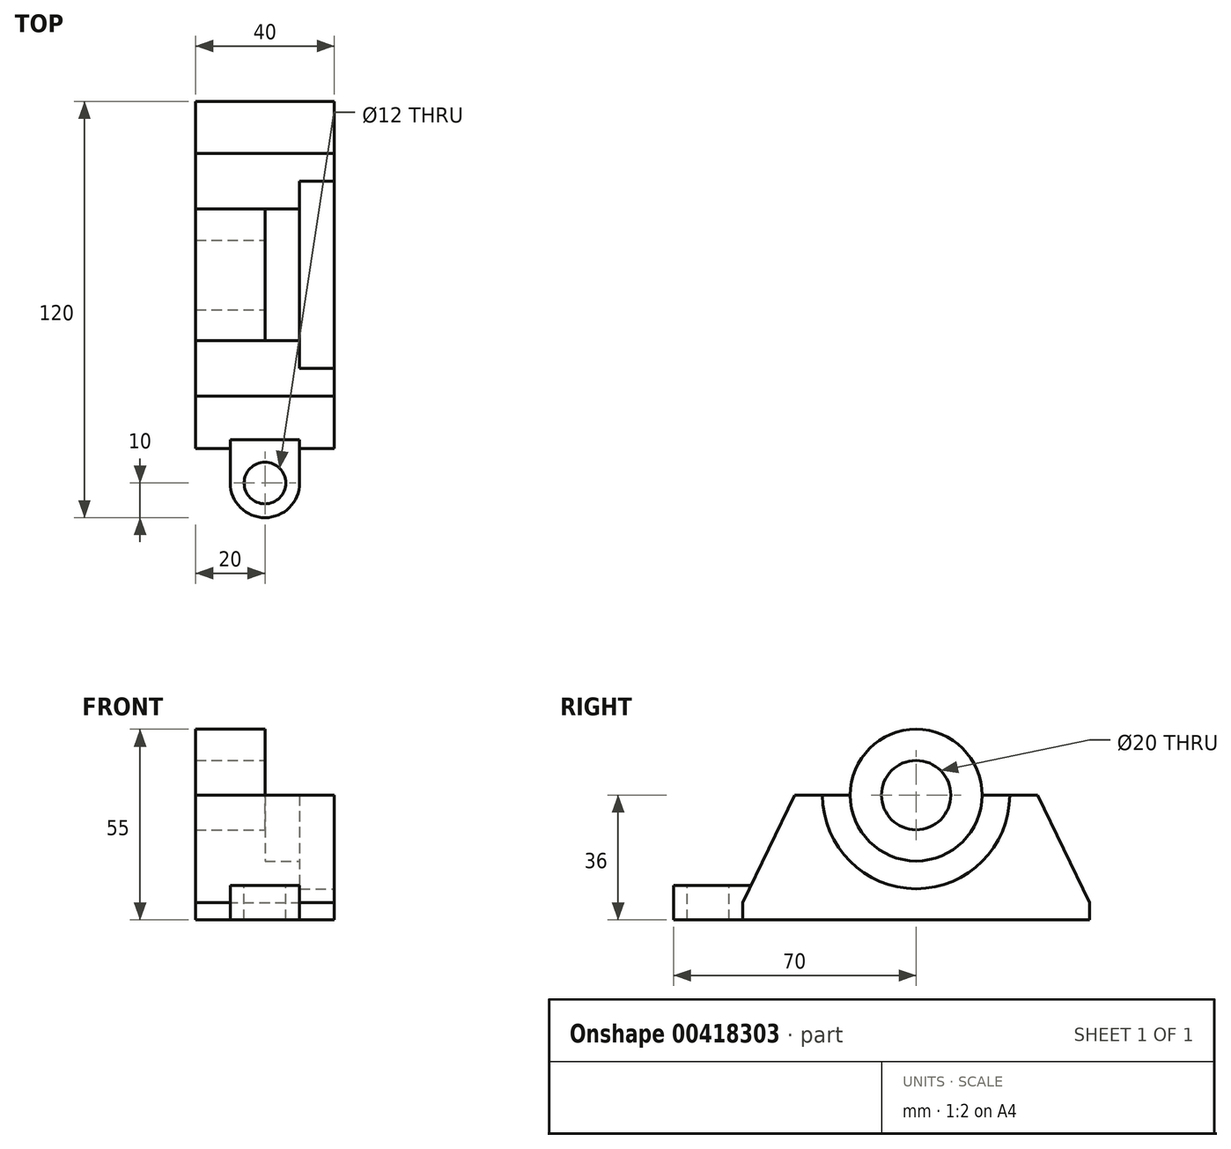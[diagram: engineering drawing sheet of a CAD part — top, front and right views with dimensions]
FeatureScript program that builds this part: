
annotation { "Feature Type Name" : "Feature", "Feature Type Description" : "" }
export const myFeature = defineFeature(function(context is Context, id is Id, definition is map)
    precondition{}
    {
        {
            var Q0;
            Q0=qCreatedBy(makeId("Right.planeOp"),FACE);
            var sketch = newSketch(context, id + "F0", { "sketchPlane" : qUnion([Q0])});
            skLineSegment(sketch, "E0.bottom", {"start": v(-50, 18) * mm, "end": v(50, 18) * mm});
            skLineSegment(sketch, "E0.top", {"start": v(-50, -18) * mm, "end": v(50, -18) * mm});
            skLineSegment(sketch, "E0.left", {"start": v(-50, 18) * mm, "end": v(-50, -18) * mm});
            skLineSegment(sketch, "E0.right", {"start": v(50, 18) * mm, "end": v(50, -18) * mm});
            skPoint(sketch, "E0.middle", {"position": v(0, 0) * mm});
            skSolve(sketch);
        }
        {
            var Q0;
            Q0 = qSketchRegion(id + "F0", true);
            extrude(context, id + "F1", {"entities" : qUnion([Q0]), "endBound" : BoundingType.SYMMETRIC, "depth" : 40 * mm});
        }
        {
            var Q0;
            Q0=makeQuery(id+"F1.opExtrude","SWEPT_FACE",FACE,{"disambiguationData":[OSD([sQuery(id+"F0.wireOp",EDGE,"E0.top")])]});
            var sketch = newSketch(context, id + "F2", { "sketchPlane" : qUnion([Q0])});
            skLineSegment(sketch, "E1.bottom", {"start": v(-10, 50) * mm, "end": v(10, 50) * mm});
            skLineSegment(sketch, "E1.top", {"start": v(-10, 70) * mm, "end": v(10, 70) * mm});
            skLineSegment(sketch, "E1.left", {"start": v(-10, 50) * mm, "end": v(-10, 70) * mm});
            skLineSegment(sketch, "E1.right", {"start": v(10, 50) * mm, "end": v(10, 70) * mm});
            skSolve(sketch);
        }
        {
            var Q0;
            Q0 = qSketchRegion(id + "F2", true);
            extrude(context, id + "F3", {"entities" : qUnion([Q0]), "operationType" : NewBodyOperationType.ADD, "oppositeDirection" : true, "depth" : 10 * mm});
        }
        {
            var Q0;
            Q0=makeQuery(id+"F3.opExtrude","SWEPT_EDGE",EDGE,{"disambiguationData":[OSD([sQuery(id+"F2.wireOp",EDGE,"E1.top"),sQuery(id+"F2.wireOp",EDGE,"E1.right")])]});
            var Q1;
            Q1=makeQuery(id+"F3.opExtrude","SWEPT_EDGE",EDGE,{"disambiguationData":[OSD([sQuery(id+"F2.wireOp",EDGE,"E1.top"),sQuery(id+"F2.wireOp",EDGE,"E1.left")])]});
            fillet(context, id + "F4", {"entities" : qUnion([Q0, Q1]), "radius" : 10 * mm, "tangentPropagation" : true, "allowEdgeOverflow" : false});
        }
        {
            var Q0;
            Q0=makeQuery(id+"F1.opExtrude","SWEPT_EDGE",EDGE,{"disambiguationData":[OSD([sQuery(id+"F0.wireOp",EDGE,"E0.bottom"),sQuery(id+"F0.wireOp",EDGE,"E0.left")])]});
            chamfer(context, id + "F5", {"entities" : qUnion([Q0]), "chamferType" : ChamferType.TWO_OFFSETS, "width1" : 15 * mm, "oppositeDirection" : true, "width2" : 31 * mm, "tangentPropagation" : true});
        }
        {
            var Q0;
            Q0=makeQuery(id+"F3.opExtrude","CAP_FACE",FACE,{"disambiguationData":[OSD([sQuery(id+"F2.wireOp",EDGE,"E1.bottom"),sQuery(id+"F2.wireOp",EDGE,"E1.top"),sQuery(id+"F2.wireOp",EDGE,"E1.left"),sQuery(id+"F2.wireOp",EDGE,"E1.right")])],"isStart":false});
            var sketch = newSketch(context, id + "F6", { "sketchPlane" : qUnion([Q0])});
            skCircle(sketch, "E2", {"center": v(0, -60) * mm, "radius": 6 * mm});
            skSolve(sketch);
        }
        {
            var Q0;
            Q0 = qSketchRegion(id + "F6", true);
            extrude(context, id + "F7", {"entities" : qUnion([Q0]), "operationType" : NewBodyOperationType.REMOVE, "endBound" : BoundingType.THROUGH_ALL, "oppositeDirection" : true, "depth" : 25 * mm});
        }
        {
            var Q0;
            Q0=makeQuery(id+"F1.opExtrude","SWEPT_EDGE",EDGE,{"disambiguationData":[OSD([sQuery(id+"F0.wireOp",EDGE,"E0.bottom"),sQuery(id+"F0.wireOp",EDGE,"E0.right")])]});
            chamfer(context, id + "F8", {"entities" : qUnion([Q0]), "chamferType" : ChamferType.TWO_OFFSETS, "width1" : 15 * mm, "oppositeDirection" : false, "width2" : 31 * mm, "tangentPropagation" : true});
        }
        {
            var Q0;
            Q0=makeQuery(id+"F1.opExtrude","CAP_FACE",FACE,{"disambiguationData":[OSD([sQuery(id+"F0.wireOp",EDGE,"E0.bottom"),sQuery(id+"F0.wireOp",EDGE,"E0.top"),sQuery(id+"F0.wireOp",EDGE,"E0.left"),sQuery(id+"F0.wireOp",EDGE,"E0.right")])],"isStart":false});
            var sketch = newSketch(context, id + "F9", { "sketchPlane" : qUnion([Q0])});
            skCircle(sketch, "E3", {"center": v(0, 18) * mm, "radius": 27 * mm});
            skSolve(sketch);
        }
        {
            var Q0;
            Q0 = qSketchRegion(id + "F9", true);
            extrude(context, id + "F10", {"entities" : qUnion([Q0]), "operationType" : NewBodyOperationType.REMOVE, "oppositeDirection" : true, "depth" : 10 * mm});
        }
        {
            var Q0;
            Q0=makeQuery(id+"F10.boolean.opBoolean","COPY",FACE,{"derivedFrom":makeQuery(id+"F10.opExtrude","CAP_FACE",FACE,{"disambiguationData":[OSD([sQuery(id+"F9.wireOp",EDGE,"E3")])],"isStart":false})});
            var sketch = newSketch(context, id + "F11", { "sketchPlane" : qUnion([Q0])});
            skCircle(sketch, "E4", {"center": v(0, 18) * mm, "radius": 19 * mm});
            skSolve(sketch);
        }
        {
            var Q0;
            Q0 = qSketchRegion(id + "F11", true);
            extrude(context, id + "F12", {"entities" : qUnion([Q0]), "operationType" : NewBodyOperationType.REMOVE, "oppositeDirection" : true, "depth" : 10 * mm});
        }
        {
            var Q0;
            Q0=makeQuery(id+"F12.boolean.opBoolean","COPY",FACE,{"derivedFrom":makeQuery(id+"F12.opExtrude","CAP_FACE",FACE,{"disambiguationData":[OSD([sQuery(id+"F11.wireOp",EDGE,"E4")])],"isStart":false})});
            var sketch = newSketch(context, id + "F13", { "sketchPlane" : qUnion([Q0])});
            skCircle(sketch, "E5", {"center": v(0, 18) * mm, "radius": 19 * mm});
            skSolve(sketch);
        }
        {
            var Q0;
            Q0 = qSketchRegion(id + "F13", true);
            extrude(context, id + "F14", {"entities" : qUnion([Q0]), "operationType" : NewBodyOperationType.ADD, "oppositeDirection" : true, "depth" : 20 * mm});
        }
        {
            var Q0;
            Q0=makeQuery(id+"F14.boolean.opBoolean","MERGE",FACE,{"derivedFrom":[makeQuery(id+"F12.boolean.opBoolean","COPY",FACE,{"derivedFrom":makeQuery(id+"F12.opExtrude","CAP_FACE",FACE,{"disambiguationData":[OSD([sQuery(id+"F11.wireOp",EDGE,"E4")])],"isStart":false})}),makeQuery(id+"F14.opExtrude","CAP_FACE",FACE,{"disambiguationData":[OSD([sQuery(id+"F13.wireOp",EDGE,"E5")])],"isStart":true})]});
            var sketch = newSketch(context, id + "F15", { "sketchPlane" : qUnion([Q0])});
            skCircle(sketch, "E6", {"center": v(0, 18) * mm, "radius": 10 * mm});
            skSolve(sketch);
        }
        {
            var Q0;
            Q0 = qSketchRegion(id + "F15", true);
            extrude(context, id + "F16", {"entities" : qUnion([Q0]), "operationType" : NewBodyOperationType.REMOVE, "endBound" : BoundingType.THROUGH_ALL, "oppositeDirection" : true, "depth" : 25 * mm});
        }
    });
